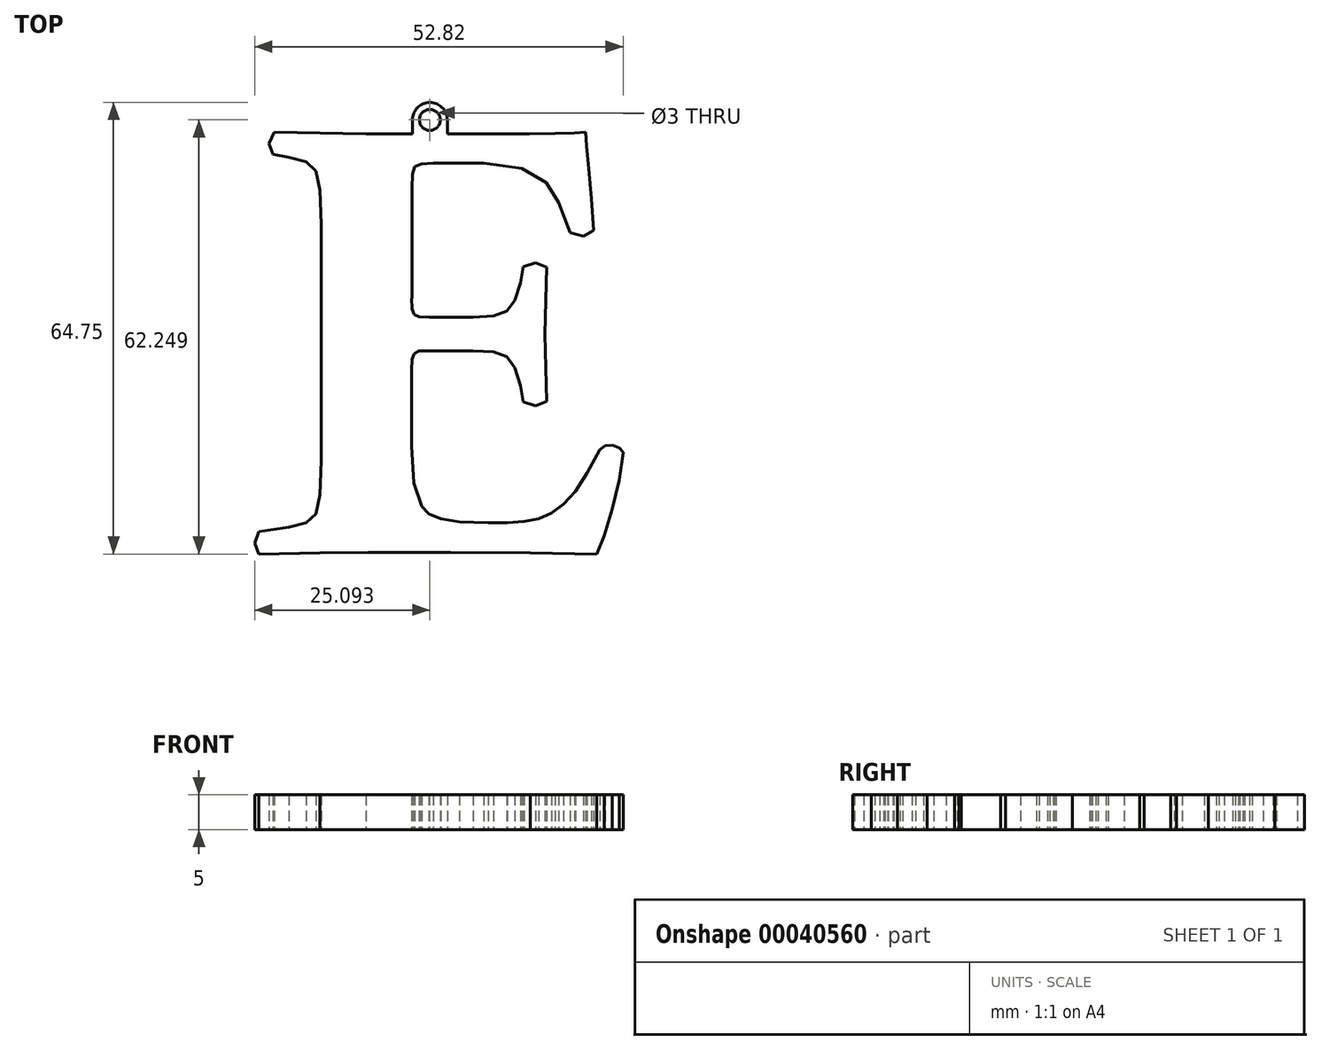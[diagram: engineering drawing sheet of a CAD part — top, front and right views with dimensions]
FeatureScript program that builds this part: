
annotation { "Feature Type Name" : "Feature", "Feature Type Description" : "" }
export const myFeature = defineFeature(function(context is Context, id is Id, definition is map)
    precondition{}
    {
        {
            var Q0;
            Q0=qCreatedBy(makeId("Top.planeOp"),FACE);
            var sketch = newSketch(context, id + "F0", { "sketchPlane" : qUnion([Q0])});
            skLineSegment(sketch, "E0", {"start": v(-3.93, 6.4) * mm, "end": v(-3.88, 4.92) * mm});
            skLineSegment(sketch, "E1", {"start": v(-3.88, 4.92) * mm, "end": v(-3.58, 4.11) * mm});
            skLineSegment(sketch, "E2", {"start": v(-3.58, 4.11) * mm, "end": v(-2.83, 3.78) * mm});
            skLineSegment(sketch, "E3", {"start": v(-2.83, 3.78) * mm, "end": v(-1.4, 3.7) * mm});
            skLineSegment(sketch, "E4", {"start": v(-1.4, 3.7) * mm, "end": v(4.92, 3.7) * mm});
            skLineSegment(sketch, "E5", {"start": v(4.92, 3.7) * mm, "end": v(7.83, 3.88) * mm});
            skLineSegment(sketch, "E6", {"start": v(7.83, 3.88) * mm, "end": v(9.7, 4.58) * mm});
            skLineSegment(sketch, "E7", {"start": v(9.7, 4.58) * mm, "end": v(10.87, 6.09) * mm});
            skLineSegment(sketch, "E8", {"start": v(10.87, 6.09) * mm, "end": v(11.66, 8.68) * mm});
            skLineSegment(sketch, "E9", {"start": v(11.66, 8.68) * mm, "end": v(12.08, 10.96) * mm});
            skLineSegment(sketch, "E10", {"start": v(12.08, 10.96) * mm, "end": v(13.86, 11.51) * mm});
            skLineSegment(sketch, "E11", {"start": v(13.86, 11.51) * mm, "end": v(15.45, 10.87) * mm});
            skLineSegment(sketch, "E12", {"start": v(15.45, 10.87) * mm, "end": v(15.2, 1.27) * mm});
            skLineSegment(sketch, "E13", {"start": v(15.2, 1.27) * mm, "end": v(15.45, -8.34) * mm});
            skLineSegment(sketch, "E14", {"start": v(15.45, -8.34) * mm, "end": v(13.86, -9.01) * mm});
            skLineSegment(sketch, "E15", {"start": v(13.86, -9.01) * mm, "end": v(12.08, -8.42) * mm});
            skLineSegment(sketch, "E16", {"start": v(12.08, -8.42) * mm, "end": v(11.66, -6.15) * mm});
            skLineSegment(sketch, "E17", {"start": v(11.66, -6.15) * mm, "end": v(10.87, -3.5) * mm});
            skLineSegment(sketch, "E18", {"start": v(10.87, -3.5) * mm, "end": v(9.7, -1.98) * mm});
            skLineSegment(sketch, "E19", {"start": v(9.7, -1.98) * mm, "end": v(7.83, -1.27) * mm});
            skLineSegment(sketch, "E20", {"start": v(7.83, -1.27) * mm, "end": v(4.92, -1.1) * mm});
            skLineSegment(sketch, "E21", {"start": v(4.92, -1.1) * mm, "end": v(-1.4, -1.1) * mm});
            skLineSegment(sketch, "E22", {"start": v(-1.4, -1.1) * mm, "end": v(-2.83, -1.15) * mm});
            skLineSegment(sketch, "E23", {"start": v(-2.83, -1.15) * mm, "end": v(-3.58, -1.47) * mm});
            skLineSegment(sketch, "E24", {"start": v(-3.58, -1.47) * mm, "end": v(-3.88, -2.3) * mm});
            skLineSegment(sketch, "E25", {"start": v(-3.88, -2.3) * mm, "end": v(-3.93, -3.88) * mm});
            skLineSegment(sketch, "E26", {"start": v(-3.93, -3.88) * mm, "end": v(-3.93, -14.74) * mm});
            skLineSegment(sketch, "E27", {"start": v(-3.93, -14.74) * mm, "end": v(-3.63, -20.06) * mm});
            skLineSegment(sketch, "E28", {"start": v(-3.63, -20.06) * mm, "end": v(-2.5, -23.42) * mm});
            skLineSegment(sketch, "E29", {"start": v(-2.5, -23.42) * mm, "end": v(-1.44, -24.47) * mm});
            skLineSegment(sketch, "E30", {"start": v(-1.44, -24.47) * mm, "end": v(0.24, -25.2) * mm});
            skLineSegment(sketch, "E31", {"start": v(0.24, -25.2) * mm, "end": v(2.93, -25.64) * mm});
            skLineSegment(sketch, "E32", {"start": v(2.93, -25.64) * mm, "end": v(7.03, -25.79) * mm});
            skLineSegment(sketch, "E33", {"start": v(7.03, -25.79) * mm, "end": v(9.78, -25.75) * mm});
            skLineSegment(sketch, "E34", {"start": v(9.78, -25.75) * mm, "end": v(12.17, -25.58) * mm});
            skLineSegment(sketch, "E35", {"start": v(12.17, -25.58) * mm, "end": v(14.26, -25.16) * mm});
            skLineSegment(sketch, "E36", {"start": v(14.26, -25.16) * mm, "end": v(16.13, -24.37) * mm});
            skLineSegment(sketch, "E37", {"start": v(16.13, -24.37) * mm, "end": v(17.87, -23.1) * mm});
            skLineSegment(sketch, "E38", {"start": v(17.87, -23.1) * mm, "end": v(19.55, -21.24) * mm});
            skLineSegment(sketch, "E39", {"start": v(19.55, -21.24) * mm, "end": v(21.24, -18.65) * mm});
            skLineSegment(sketch, "E40", {"start": v(21.24, -18.65) * mm, "end": v(23.04, -15.25) * mm});
            skLineSegment(sketch, "E41", {"start": v(23.04, -15.25) * mm, "end": v(23.83, -14.74) * mm});
            skLineSegment(sketch, "E42", {"start": v(23.83, -14.74) * mm, "end": v(24.87, -14.67) * mm});
            skLineSegment(sketch, "E43", {"start": v(24.87, -14.67) * mm, "end": v(25.84, -15) * mm});
            skLineSegment(sketch, "E44", {"start": v(25.84, -15) * mm, "end": v(26.4, -15.67) * mm});
            skLineSegment(sketch, "E45", {"start": v(26.4, -15.67) * mm, "end": v(25.85, -19.6) * mm});
            skLineSegment(sketch, "E46", {"start": v(25.85, -19.6) * mm, "end": v(24.86, -23.81) * mm});
            skLineSegment(sketch, "E47", {"start": v(24.86, -23.81) * mm, "end": v(23.7, -27.6) * mm});
            skLineSegment(sketch, "E48", {"start": v(23.7, -27.6) * mm, "end": v(22.62, -30.25) * mm});
            skLineSegment(sketch, "E49", {"start": v(22.62, -30.25) * mm, "end": v(13.1, -30.06) * mm});
            skLineSegment(sketch, "E50", {"start": v(13.1, -30.06) * mm, "end": v(1.63, -30) * mm});
            skLineSegment(sketch, "E51", {"start": v(1.63, -30) * mm, "end": v(-10.16, -30) * mm});
            skLineSegment(sketch, "E52", {"start": v(-10.16, -30) * mm, "end": v(-17.08, -30.06) * mm});
            skLineSegment(sketch, "E53", {"start": v(-17.08, -30.06) * mm, "end": v(-25.84, -30.25) * mm});
            skLineSegment(sketch, "E54", {"start": v(-25.84, -30.25) * mm, "end": v(-26.4, -28.65) * mm});
            skLineSegment(sketch, "E55", {"start": v(-26.4, -28.65) * mm, "end": v(-25.84, -27.05) * mm});
            skLineSegment(sketch, "E56", {"start": v(-25.84, -27.05) * mm, "end": v(-21.54, -26.37) * mm});
            skLineSegment(sketch, "E57", {"start": v(-21.54, -26.37) * mm, "end": v(-19.08, -25.77) * mm});
            skLineSegment(sketch, "E58", {"start": v(-19.08, -25.77) * mm, "end": v(-17.68, -24.49) * mm});
            skLineSegment(sketch, "E59", {"start": v(-17.68, -24.49) * mm, "end": v(-17.05, -21.76) * mm});
            skLineSegment(sketch, "E60", {"start": v(-17.05, -21.76) * mm, "end": v(-16.9, -16.85) * mm});
            skLineSegment(sketch, "E61", {"start": v(-16.9, -16.85) * mm, "end": v(-16.9, 17.02) * mm});
            skLineSegment(sketch, "E62", {"start": v(-16.9, 17.02) * mm, "end": v(-17.05, 21.9) * mm});
            skLineSegment(sketch, "E63", {"start": v(-17.05, 21.9) * mm, "end": v(-17.68, 24.64) * mm});
            skLineSegment(sketch, "E64", {"start": v(-17.68, 24.64) * mm, "end": v(-19.08, 25.97) * mm});
            skLineSegment(sketch, "E65", {"start": v(-19.08, 25.97) * mm, "end": v(-21.54, 26.63) * mm});
            skLineSegment(sketch, "E66", {"start": v(-21.54, 26.63) * mm, "end": v(-23.82, 27.05) * mm});
            skLineSegment(sketch, "E67", {"start": v(-23.82, 27.05) * mm, "end": v(-24.4, 28.62) * mm});
            skLineSegment(sketch, "E68", {"start": v(-24.4, 28.62) * mm, "end": v(-23.65, 30.25) * mm});
            skLineSegment(sketch, "E69", {"start": v(-23.65, 30.25) * mm, "end": v(-10.5, 30) * mm});
            skLineSegment(sketch, "E70", {"start": v(-10.5, 30) * mm, "end": v(8.8, 30) * mm});
            skLineSegment(sketch, "E71", {"start": v(8.8, 30) * mm, "end": v(13, 30.02) * mm});
            skLineSegment(sketch, "E72", {"start": v(13, 30.02) * mm, "end": v(16.64, 30.06) * mm});
            skLineSegment(sketch, "E73", {"start": v(16.64, 30.06) * mm, "end": v(19.42, 30.14) * mm});
            skLineSegment(sketch, "E74", {"start": v(19.42, 30.14) * mm, "end": v(21.01, 30.25) * mm});
            skLineSegment(sketch, "E75", {"start": v(21.01, 30.25) * mm, "end": v(21.17, 28.3) * mm});
            skLineSegment(sketch, "E76", {"start": v(21.17, 28.3) * mm, "end": v(21.47, 24.95) * mm});
            skLineSegment(sketch, "E77", {"start": v(21.47, 24.95) * mm, "end": v(21.84, 20.74) * mm});
            skLineSegment(sketch, "E78", {"start": v(21.84, 20.74) * mm, "end": v(22.2, 16.18) * mm});
            skLineSegment(sketch, "E79", {"start": v(22.2, 16.18) * mm, "end": v(20.73, 15.32) * mm});
            skLineSegment(sketch, "E80", {"start": v(20.73, 15.32) * mm, "end": v(18.82, 15.84) * mm});
            skLineSegment(sketch, "E81", {"start": v(18.82, 15.84) * mm, "end": v(17.16, 20.15) * mm});
            skLineSegment(sketch, "E82", {"start": v(17.16, 20.15) * mm, "end": v(15.36, 23) * mm});
            skLineSegment(sketch, "E83", {"start": v(15.36, 23) * mm, "end": v(11.91, 25.06) * mm});
            skLineSegment(sketch, "E84", {"start": v(11.91, 25.06) * mm, "end": v(6.43, 25.79) * mm});
            skLineSegment(sketch, "E85", {"start": v(6.43, 25.79) * mm, "end": v(-0.81, 25.79) * mm});
            skLineSegment(sketch, "E86", {"start": v(-0.81, 25.79) * mm, "end": v(-2.57, 25.7) * mm});
            skLineSegment(sketch, "E87", {"start": v(-2.57, 25.7) * mm, "end": v(-3.47, 25.28) * mm});
            skLineSegment(sketch, "E88", {"start": v(-3.47, 25.28) * mm, "end": v(-3.8, 24.22) * mm});
            skLineSegment(sketch, "E89", {"start": v(-3.8, 24.22) * mm, "end": v(-3.84, 22.24) * mm});
            skLineSegment(sketch, "E90", {"start": v(-3.84, 22.24) * mm, "end": v(-3.84, 6.4) * mm});
            skLineSegment(sketch, "E91", {"start": v(-3.84, 6.4) * mm, "end": v(-3.93, 6.4) * mm});
            skSolve(sketch);
        }
        {
            var Q0;
            Q0=makeQuery(id+"F0.imprint","IMPRINT",FACE,{"disambiguationData":[TD([[makeQuery(id+"F0.imprint","IMPRINT",EDGE,{"derivedFrom":sQuery(id+"F0.wireOp",EDGE,"E0")}),-1.0]])]});
            extrude(context, id + "F1", {"entities" : qUnion([Q0]), "depth" : 5 * mm});
        }
        {
            var Q0;
            Q0=qCreatedBy(makeId("Top.planeOp"),FACE);
            var sketch = newSketch(context, id + "F2", { "sketchPlane" : qUnion([Q0])});
            skLineSegment(sketch, "E92.bottom", {"start": v(-3.82, 32) * mm, "end": v(1.18, 32) * mm});
            skLineSegment(sketch, "E92.top", {"start": v(-3.82, 30) * mm, "end": v(1.18, 30) * mm});
            skLineSegment(sketch, "E92.left", {"start": v(-3.82, 32) * mm, "end": v(-3.82, 30) * mm});
            skLineSegment(sketch, "E92.right", {"start": v(1.18, 32) * mm, "end": v(1.18, 30) * mm});
            skArc(sketch, "E93", {"start": v(1.18, 32) * mm, "mid": v(-1.32, 34.5) * mm, "end": v(-3.82, 32) * mm});
            skCircle(sketch, "E94", {"center": v(-1.32, 32) * mm, "radius": 1.5 * mm});
            skSolve(sketch);
        }
        {
            var Q0;
            Q0 = qSketchRegion(id + "F2", true);
            extrude(context, id + "F3", {"entities" : qUnion([Q0]), "operationType" : NewBodyOperationType.ADD, "depth" : 5 * mm});
        }
    });
